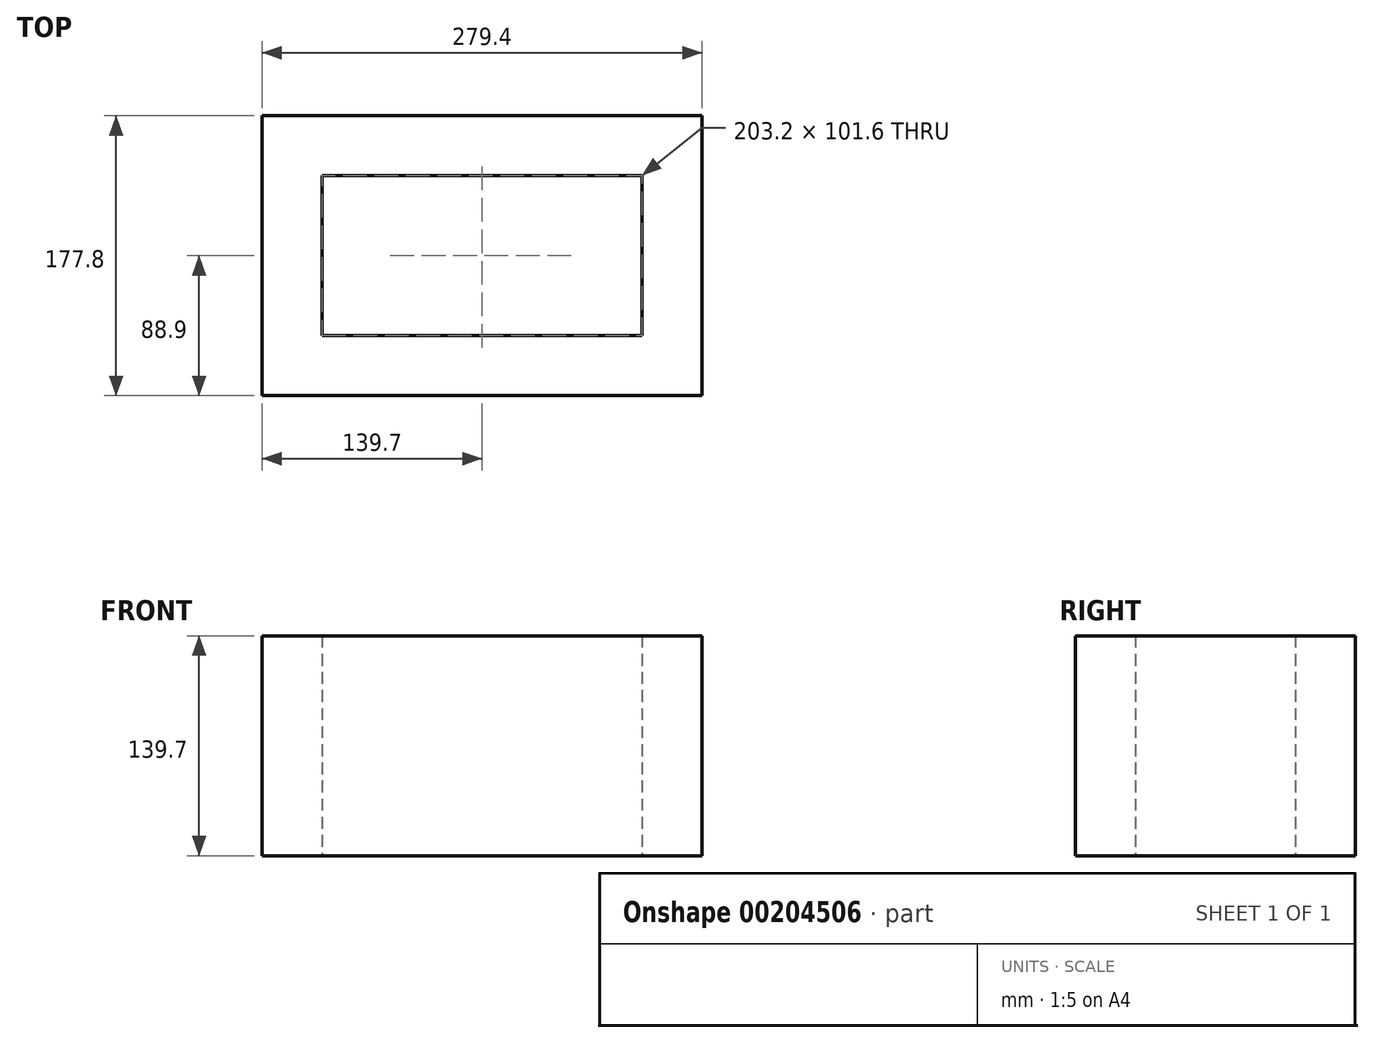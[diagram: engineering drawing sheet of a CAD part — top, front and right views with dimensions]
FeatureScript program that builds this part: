
annotation { "Feature Type Name" : "Feature", "Feature Type Description" : "" }
export const myFeature = defineFeature(function(context is Context, id is Id, definition is map)
    precondition{}
    {
        {
            var Q0;
            Q0=qCreatedBy(makeId("Top.planeOp"),FACE);
            var sketch = newSketch(context, id + "F0", { "sketchPlane" : qUnion([Q0])});
            skLineSegment(sketch, "E0.bottom", {"start": v(101.6, -50.8) * mm, "end": v(-101.6, -50.8) * mm});
            skLineSegment(sketch, "E0.top", {"start": v(101.6, 50.8) * mm, "end": v(-101.6, 50.8) * mm});
            skLineSegment(sketch, "E0.left", {"start": v(101.6, -50.8) * mm, "end": v(101.6, 50.8) * mm});
            skLineSegment(sketch, "E0.right", {"start": v(-101.6, -50.8) * mm, "end": v(-101.6, 50.8) * mm});
            skPoint(sketch, "E0.middle", {"position": v(0, 0) * mm});
            skSolve(sketch);
        }
        {
            var Q0;
            Q0=makeQuery(id+"F0.imprint","IMPRINT",FACE,{"disambiguationData":[TD([[makeQuery(id+"F0.imprint","IMPRINT",EDGE,{"derivedFrom":sQuery(id+"F0.wireOp",EDGE,"E0.bottom")}),-1.0]])]});
            extrude(context, id + "F1", {"entities" : qUnion([Q0]), "depth" : 139.7 * mm});
        }
        {
            var Q0;
            Q0=makeQuery(id+"F1.opExtrude","CAP_FACE",FACE,{"disambiguationData":[OSD([sQuery(id+"F0.wireOp",EDGE,"E0.bottom"),sQuery(id+"F0.wireOp",EDGE,"E0.top"),sQuery(id+"F0.wireOp",EDGE,"E0.left"),sQuery(id+"F0.wireOp",EDGE,"E0.right")])],"isStart":false});
            var Q1;
            Q1=makeQuery(id+"F1.opExtrude","CAP_FACE",FACE,{"disambiguationData":[OSD([sQuery(id+"F0.wireOp",EDGE,"E0.bottom"),sQuery(id+"F0.wireOp",EDGE,"E0.top"),sQuery(id+"F0.wireOp",EDGE,"E0.left"),sQuery(id+"F0.wireOp",EDGE,"E0.right")])],"isStart":true});
            shell(context, id + "F2", {"entities" : qUnion([Q0, Q1]), "thickness" : 38.1 * mm, "oppositeDirection" : true});
        }
    });
